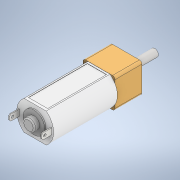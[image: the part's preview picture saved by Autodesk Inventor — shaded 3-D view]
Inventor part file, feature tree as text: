
AUTODESK INVENTOR PART (.ipt)
format: ipt  version: 2021 (Build 250183000, 183)  size: 159,744 bytes
history: imported  units: in
note: dims shown in document units (in); Inventor stores cm internally (conversion verified against a paired STEP export)
features: imported_body x1
ambient origin geometry x8: Origin, YZ Plane, XZ Plane, XY Plane, X Axis, Y Axis, Z Axis, Center Point
bodies: Solid1 (imported_parasolid), Body1 (imported_parasolid)
feature tree (1):
  imported_body  NMx_Import_Brep_tag  [imported B-rep: ~58 faces, bbox_mm=[13.557015, 12.1, 52.7]]
